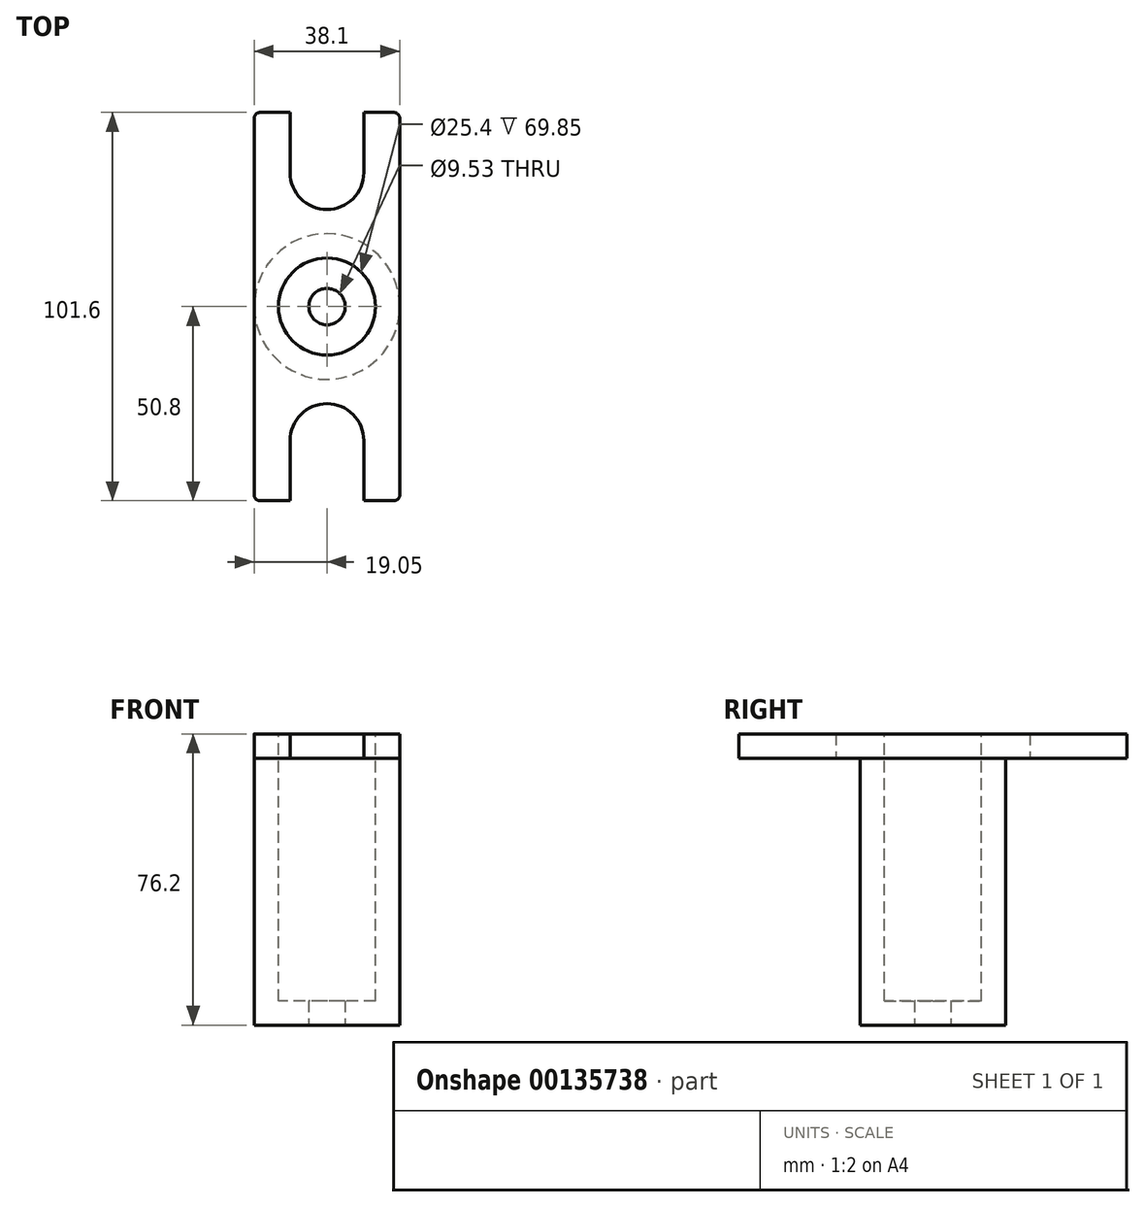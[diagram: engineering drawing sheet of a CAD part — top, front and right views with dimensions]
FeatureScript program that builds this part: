
annotation { "Feature Type Name" : "Feature", "Feature Type Description" : "" }
export const myFeature = defineFeature(function(context is Context, id is Id, definition is map)
    precondition{}
    {
        {
            var Q0;
            Q0=qCreatedBy(makeId("Top.planeOp"),FACE);
            var sketch = newSketch(context, id + "F0", { "sketchPlane" : qUnion([Q0])});
            skCircle(sketch, "E0", {"center": v(0, 0) * mm, "radius": 19.05 * mm});
            skSolve(sketch);
        }
        {
            var Q0;
            Q0=makeQuery(id+"F0.imprint","IMPRINT",FACE,{"disambiguationData":[TD([[makeQuery(id+"F0.imprint","IMPRINT",EDGE,{"derivedFrom":sQuery(id+"F0.wireOp",EDGE,"E0")}),1.0]])]});
            extrude(context, id + "F1", {"entities" : qUnion([Q0]), "depth" : 69.85 * mm});
        }
        {
            var Q0;
            Q0=makeQuery(id+"F1.opExtrude","CAP_FACE",FACE,{"disambiguationData":[OSD([sQuery(id+"F0.wireOp",EDGE,"E0")])],"isStart":false});
            var sketch = newSketch(context, id + "F2", { "sketchPlane" : qUnion([Q0])});
            skCircle(sketch, "E1", {"center": v(0, 0) * mm, "radius": 12.7 * mm});
            skSolve(sketch);
        }
        {
            var Q0;
            Q0 = qSketchRegion(id + "F2", true);
            extrude(context, id + "F3", {"entities" : qUnion([Q0]), "operationType" : NewBodyOperationType.REMOVE, "oppositeDirection" : true, "depth" : 63.5 * mm});
        }
        {
            var Q0;
            Q0=makeQuery(id+"F1.opExtrude","CAP_FACE",FACE,{"disambiguationData":[OSD([sQuery(id+"F0.wireOp",EDGE,"E0")])],"isStart":true});
            var sketch = newSketch(context, id + "F4", { "sketchPlane" : qUnion([Q0])});
            skCircle(sketch, "E2", {"center": v(0, 0) * mm, "radius": 4.76 * mm});
            skSolve(sketch);
        }
        {
            var Q0;
            Q0=makeQuery(id+"F4.imprint","IMPRINT",FACE,{"disambiguationData":[TD([[makeQuery(id+"F4.imprint","IMPRINT",EDGE,{"derivedFrom":sQuery(id+"F4.wireOp",EDGE,"E2")}),1.0]])]});
            extrude(context, id + "F5", {"entities" : qUnion([Q0]), "operationType" : NewBodyOperationType.REMOVE, "endBound" : BoundingType.THROUGH_ALL, "oppositeDirection" : true, "depth" : 25.4 * mm});
        }
        {
            var Q0;
            Q0=makeQuery(id+"F1.opExtrude","CAP_FACE",FACE,{"disambiguationData":[OSD([sQuery(id+"F0.wireOp",EDGE,"E0")])],"isStart":false});
            var sketch = newSketch(context, id + "F6", { "sketchPlane" : qUnion([Q0])});
            skLineSegment(sketch, "E3.left", {"start": v(-19.05, 49.27) * mm, "end": v(-19.05, -49.28) * mm});
            skLineSegment(sketch, "E3.right", {"start": v(19.05, 49.28) * mm, "end": v(19.05, -49.28) * mm});
            skLineSegment(sketch, "E4", {"start": v(-24.9, 0) * mm, "end": v(30.26, 0) * mm, "construction": true});
            skLineSegment(sketch, "E5", {"start": v(0, 46.28) * mm, "end": v(0, -40.42) * mm, "construction": true});
            skPoint(sketch, "E6.visualSharp", {"position": v(-19.05, 50.8) * mm});
            skArc(sketch, "E6.filletArc", {"start": v(-17.53, 50.8) * mm, "mid": v(-18.6, 50.34) * mm, "end": v(-19.05, 49.27) * mm});
            skPoint(sketch, "E7.visualSharp", {"position": v(19.05, 50.8) * mm});
            skArc(sketch, "E7.filletArc", {"start": v(19.05, 49.28) * mm, "mid": v(18.6, 50.35) * mm, "end": v(17.53, 50.8) * mm});
            skPoint(sketch, "E8.visualSharp", {"position": v(19.05, -50.8) * mm});
            skArc(sketch, "E8.filletArc", {"start": v(17.53, -50.8) * mm, "mid": v(18.6, -50.35) * mm, "end": v(19.05, -49.28) * mm});
            skPoint(sketch, "E9.visualSharp", {"position": v(-19.05, -50.8) * mm});
            skArc(sketch, "E9.filletArc", {"start": v(-19.05, -49.28) * mm, "mid": v(-18.6, -50.35) * mm, "end": v(-17.53, -50.8) * mm});
            skLineSegment(sketch, "E10", {"start": v(-17.53, 50.8) * mm, "end": v(-9.65, 50.8) * mm});
            skLineSegment(sketch, "E11", {"start": v(17.53, 50.8) * mm, "end": v(9.65, 50.8) * mm});
            skLineSegment(sketch, "E12", {"start": v(-9.65, 50.8) * mm, "end": v(-9.65, 35.05) * mm});
            skLineSegment(sketch, "E13", {"start": v(9.65, 50.8) * mm, "end": v(9.65, 35.05) * mm});
            skArc(sketch, "E14", {"start": v(-9.65, 35.05) * mm, "mid": v(0, 25.4) * mm, "end": v(9.65, 35.05) * mm});
            skLineSegment(sketch, "E15", {"start": v(-17.53, -50.8) * mm, "end": v(-9.65, -50.8) * mm});
            skLineSegment(sketch, "E16", {"start": v(-9.65, -50.8) * mm, "end": v(-9.65, -35.05) * mm});
            skLineSegment(sketch, "E17", {"start": v(17.53, -50.8) * mm, "end": v(9.65, -50.8) * mm});
            skLineSegment(sketch, "E18", {"start": v(9.65, -50.8) * mm, "end": v(9.65, -35.05) * mm});
            skArc(sketch, "E19", {"start": v(9.65, -35.05) * mm, "mid": v(0, -25.4) * mm, "end": v(-9.65, -35.05) * mm});
            skSolve(sketch);
        }
        {
            var Q0;
            Q0 = qSketchRegion(id + "F6", true);
            extrude(context, id + "F7", {"entities" : qUnion([Q0]), "operationType" : NewBodyOperationType.ADD, "depth" : 6.35 * mm});
        }
        {
            var Q0;
            Q0=makeQuery(id+"F7.opExtrude","CAP_FACE",FACE,{"disambiguationData":[OSD([sQuery(id+"F6.wireOp",EDGE,"E3.left"),sQuery(id+"F6.wireOp",EDGE,"E3.right"),sQuery(id+"F6.wireOp",EDGE,"E6.filletArc"),sQuery(id+"F6.wireOp",EDGE,"E7.filletArc"),sQuery(id+"F6.wireOp",EDGE,"E8.filletArc"),sQuery(id+"F6.wireOp",EDGE,"E9.filletArc"),sQuery(id+"F6.wireOp",EDGE,"E10"),sQuery(id+"F6.wireOp",EDGE,"E11"),sQuery(id+"F6.wireOp",EDGE,"E12"),sQuery(id+"F6.wireOp",EDGE,"E13"),sQuery(id+"F6.wireOp",EDGE,"E14"),sQuery(id+"F6.wireOp",EDGE,"E15"),sQuery(id+"F6.wireOp",EDGE,"E16"),sQuery(id+"F6.wireOp",EDGE,"E17"),sQuery(id+"F6.wireOp",EDGE,"E18"),sQuery(id+"F6.wireOp",EDGE,"E19")])],"isStart":false});
            var sketch = newSketch(context, id + "F8", { "sketchPlane" : qUnion([Q0])});
            skCircle(sketch, "E20", {"center": v(0, 0) * mm, "radius": 12.7 * mm});
            skSolve(sketch);
        }
        {
            var Q0;
            Q0 = qSketchRegion(id + "F8", true);
            extrude(context, id + "F9", {"entities" : qUnion([Q0]), "operationType" : NewBodyOperationType.REMOVE, "oppositeDirection" : true, "depth" : 6.35 * mm});
        }
    });
